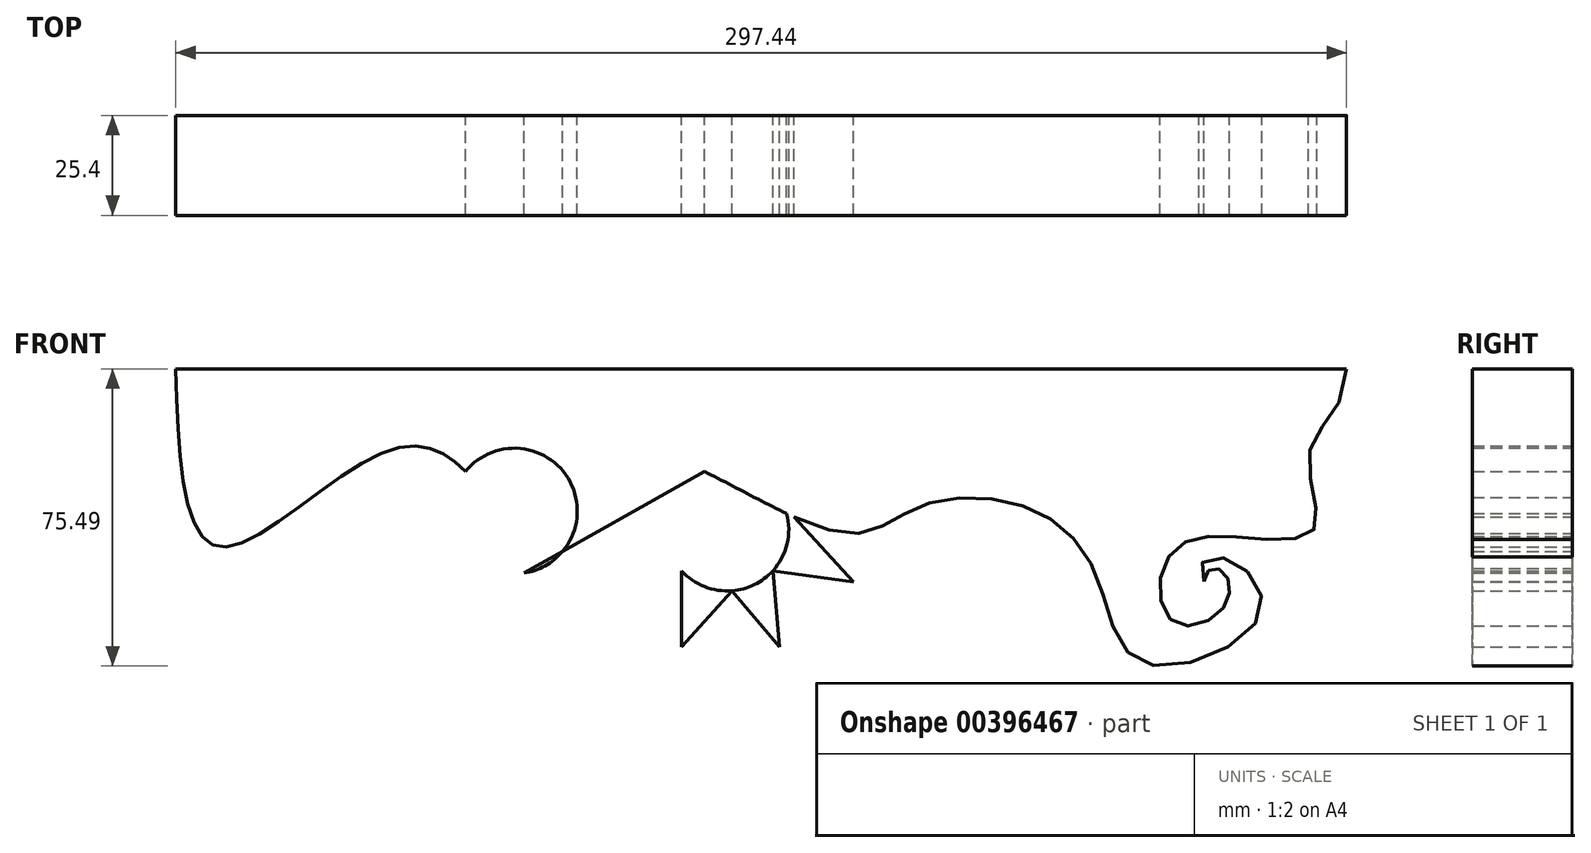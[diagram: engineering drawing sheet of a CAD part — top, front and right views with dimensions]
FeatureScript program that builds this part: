
annotation { "Feature Type Name" : "Feature", "Feature Type Description" : "" }
export const myFeature = defineFeature(function(context is Context, id is Id, definition is map)
    precondition{}
    {
        {
            var Q0;
            Q0=qCreatedBy(makeId("Front.planeOp"),FACE);
            var sketch = newSketch(context, id + "F0", { "sketchPlane" : qUnion([Q0])});
            skLineSegment(sketch, "E0", {"start": v(-149.81, 34.93) * mm, "end": v(147.63, 34.93) * mm});
            skFitSpline(sketch, "E1", {"points": [v(-149.81, 34.93) * mm, v(-138.7, -10.22) * mm, v(-96.26, 14.05) * mm, v(-76.2, 8.85) * mm], "startDerivative": vector(4.51, -175.82) * mm, "endDerivative": vector(55.9, -60.71) * mm});
            skArc(sketch, "E2", {"start": v(-61.33, -16.96) * mm, "mid": v(-49.94, 6.8) * mm, "end": v(-76.2, 8.85) * mm});
            skLineSegment(sketch, "E3", {"start": v(-61.33, -16.96) * mm, "end": v(-15.5, 8.85) * mm});
            skFitSpline(sketch, "E4", {"points": [v(-15.5, 8.85) * mm, v(22.52, -6.89) * mm, v(39.22, 0) * mm, v(65.81, 0) * mm, v(83.85, -17) * mm, v(96.28, -39.86) * mm, v(125.96, -26.45) * mm, v(114.91, -12.88) * mm, v(111.4, -19.1) * mm], "startDerivative": vector(228.41, -111.5) * mm, "endDerivative": vector(131.7, -153.1) * mm});
            skFitSpline(sketch, "E5", {"points": [v(111.4, -19.1) * mm, v(113, -15.98) * mm, v(116.25, -16.47) * mm, v(117.89, -21.13) * mm, v(114.91, -27.3) * mm, v(104.88, -29.99) * mm, v(100.16, -20.59) * mm, v(105.9, -9.47) * mm, v(124.04, -8.1) * mm, v(139.65, -5.4) * mm, v(138.17, 13.85) * mm, v(147.63, 34.93) * mm], "startDerivative": vector(18.5, 76) * mm, "endDerivative": vector(-5.48, 238.53) * mm});
            skPoint(sketch, "E6", {"position": v(-29.97, 0) * mm});
            skPoint(sketch, "E7", {"position": v(-104.65, 77.34) * mm});
            skArc(sketch, "E8", {"start": v(-25.27, -4.19) * mm, "mid": v(-8.49, -21.42) * mm, "end": v(5.4, -1.78) * mm});
            skLineSegment(sketch, "E9", {"start": v(-21.3, -16.34) * mm, "end": v(-41.59, -22.67) * mm});
            skLineSegment(sketch, "E10", {"start": v(-41.59, -22.67) * mm, "end": v(-34.35, -12.87) * mm});
            skLineSegment(sketch, "E11", {"start": v(-21.3, -16.34) * mm, "end": v(-21.3, -35.68) * mm});
            skLineSegment(sketch, "E12", {"start": v(-21.3, -35.68) * mm, "end": v(-8.49, -21.42) * mm});
            skLineSegment(sketch, "E13", {"start": v(-8.49, -21.42) * mm, "end": v(3.55, -35.68) * mm});
            skLineSegment(sketch, "E14", {"start": v(3.55, -35.68) * mm, "end": v(1.87, -16.34) * mm});
            skLineSegment(sketch, "E15", {"start": v(1.87, -16.34) * mm, "end": v(22.31, -19.16) * mm});
            skLineSegment(sketch, "E16", {"start": v(22.31, -19.16) * mm, "end": v(7.29, -2.64) * mm});
            skSolve(sketch);
        }
        {
            var Q0;
            Q0=sQuery(id+"F0.wireOp",EDGE,"E4");
            extrude(context, id + "F1", {"bodyType" : ToolBodyType.SURFACE, "surfaceEntities" : qUnion([Q0]), "depth" : 25.4 * mm});
        }
        {
            var Q0;
            Q0 = qSketchRegion(id + "F0", true);
            extrude(context, id + "F2", {"entities" : qUnion([Q0]), "depth" : 25.4 * mm});
        }
        {
            var Q0;
            Q0 = qSketchRegion(id + "F0", true);
            extrude(context, id + "F3", {"entities" : qUnion([Q0]), "depth" : 25.4 * mm});
        }
        {
            var Q0;
            Q0 = qSketchRegion(id + "F0", true);
            extrude(context, id + "F4", {"entities" : qUnion([Q0]), "depth" : 25.4 * mm});
        }
    });
